# Revit family: NBS_Allermuir_DmstcChrs-en-us-Tarry_Footstool
name_source: partatom
category: Furniture
revit_build: Autodesk Revit 2017 (Build: 20181011_1645(x64)
units: mm (PartAtom-declared; Revit-internal decimal feet)

## family parameters
Always vertical = Yes
Cut with Voids When Loaded = No
Room Calculation Point = No
Shared = No
Work Plane-Based = No

## types (2) — shared parameters
AssetType = Movable
Category = Pr_40_50_12_22:Dining chairs
DurationUnit = year
ExpectedLife = 10
IfcExportAs = IfcFurnitureType
IfcExportType = CHAIR
IsBuiltIn = No
ManufacturerName = Allermuir
ManufacturerURL = http://www.allermuir.com
NBSCertification = www.nationalbimlibrary.com/cert/egfdxkbk
NBSDescription = Domestic chairs
NBSReference = 45-35-20/365
NominalHeight = 16 "
NominalLength = 24 "
OmniClassCode = 22-12 52 13
OmniClassTitle = Chairs
OmniClassVersion = Table 22 2012-05-16
ProductInformation = http://www.allermuir.com
SeatBaseMaterial = NBS_Concept
SeatingHeight = 16 "
SeatingSeatMaterial = NBS_Concept
SeatsAndBacksFinish = Upholstered
SeatsAndBacksMaterial = Upholstered
Status = New
Style = Footstool
Uniclass2015Code = Pr_40_50_12_22
Uniclass2015Title = Dining chairs
Uniclass2015Version = Products v1.12
Version = 1
WarrantyDescription = Allermuir warrant that its manufactured products are free from manufacturing defects - in materials or workmanship - for a period of five (5) years. , Allermuir will repair, or replace (at Allermuir's sole discretion) with comparable free of charge materials / components, any product / component which fails under normal use in a single shift environment, as a result of a defect in the materials and/ or workmanship
WarrantyDurationParts = 5
WarrantyDurationUnit = year
zero-valued in all types: HighestSeatingHeight, LowestSeatingHeight

## per-type parameters (varying)
| type | BIMObjectName | Description | Features | FramesColour | FramesFinish | FramesMaterial | Has4StarBase | HasWoodLegs | ModelReference | Name | NominalDepth | NominalWidth | Size |
| TARFS03 | NBS_Allermuir_DomesticChairs_TarryFootstool_TARFS03_US | Footstool with wood legs | Fully upholstered, Solid ash legs with clear finish, Plastic Glides, Optional feature: solid ash legs can be stained or color washed, Optional feature: plastic glides with felt, Optional feature: Two tone upholstery |  | Clear | Solid ash | No | Yes | TarryFootstool_TARFS03 | DomesticChairs_TarryFootstool_TARFS03_Allermuir | 18 " | 24 " | 24.25 x 16.25 x 19.5 " |
| TARFS05 | NBS_Allermuir_DomesticChairs_TarryFootstool_TARFS05_US | Footstool on a four star base | Fully upholstered,, 4-star blade base finished in black powder coat, plastic glides, Optional feature: 4-star blade base available in ceramic white powder coat, Optional feature: Two Tone Upholstery | Black | Powder coat | Steel powder coated | Yes | No | TarryFootstool_TARFS05 | DomesticChairs_TarryFootstool_TARFS05_Allermuir | 20 " | 25 " | 24.5" x 16.25" x 18.25 " |

note: column(s) folded — value = type name in every type: ModelNumber

## geometry (parser evidence)
native form markers: Sweep x2
no freeform markers — native parametric forms only
